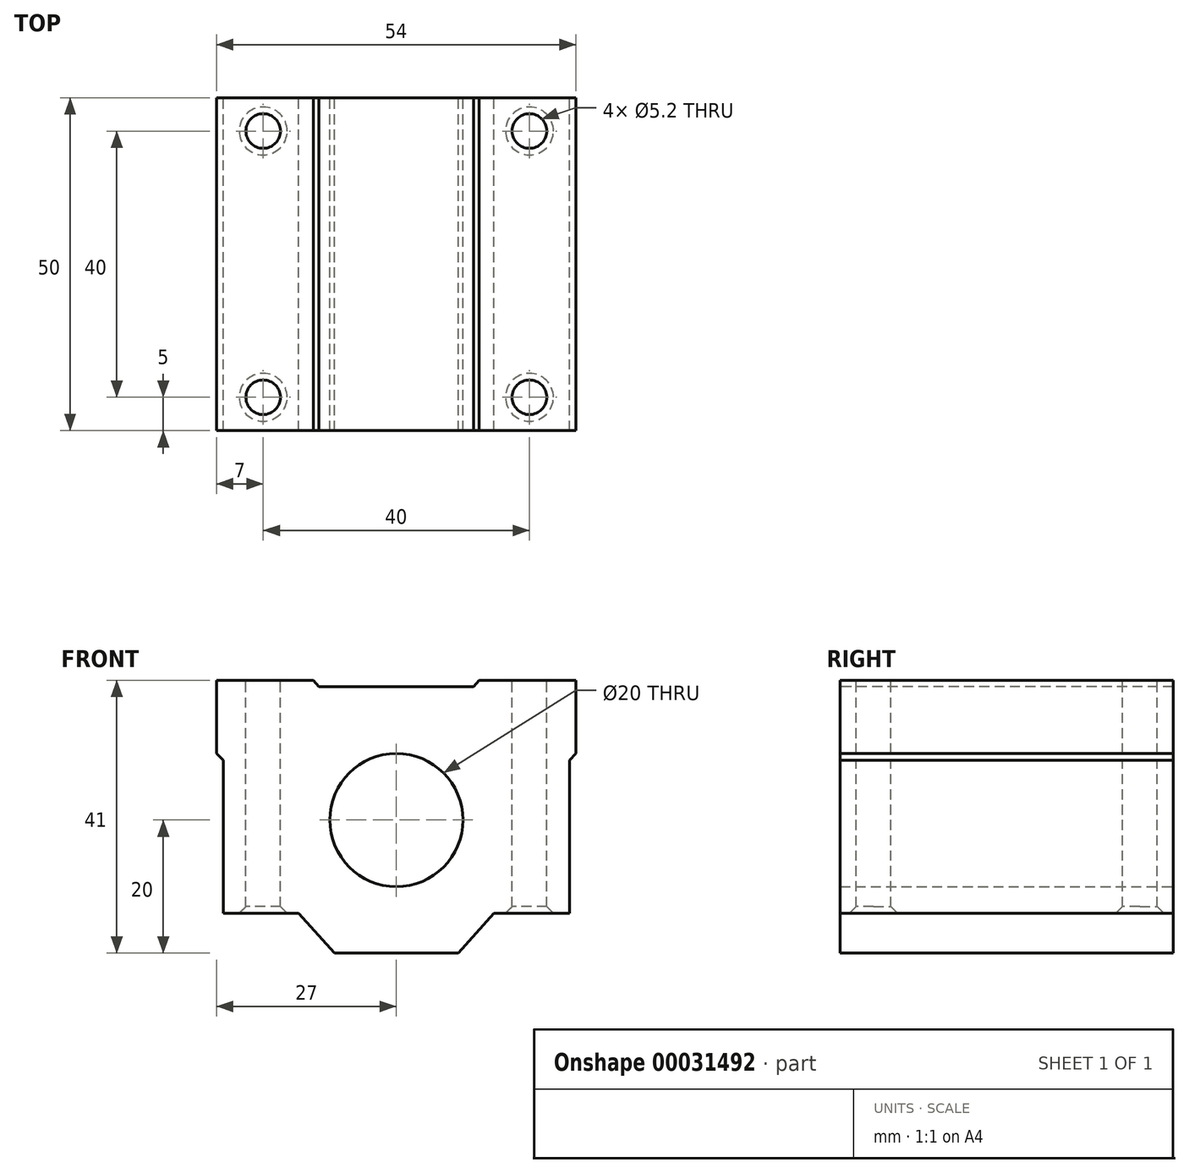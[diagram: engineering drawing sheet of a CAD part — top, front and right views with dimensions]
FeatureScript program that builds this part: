
annotation { "Feature Type Name" : "Feature", "Feature Type Description" : "" }
export const myFeature = defineFeature(function(context is Context, id is Id, definition is map)
    precondition{}
    {
        {
            var Q0;
            Q0=qCreatedBy(makeId("Front.planeOp"),FACE);
            var sketch = newSketch(context, id + "F0", { "sketchPlane" : qUnion([Q0])});
            skCircle(sketch, "E0", {"center": v(0, 0) * mm, "radius": 10 * mm});
            skLineSegment(sketch, "E1.rect.bottom", {"start": v(27, 21) * mm, "end": v(-27, 21) * mm});
            skLineSegment(sketch, "E1.rect.top", {"start": v(27, -20) * mm, "end": v(-27, -20) * mm});
            skLineSegment(sketch, "E1.rect.left", {"start": v(27, 21) * mm, "end": v(27, -20) * mm});
            skLineSegment(sketch, "E1.rect.right", {"start": v(-27, 21) * mm, "end": v(-27, -20) * mm});
            skPoint(sketch, "E1.rect.middle", {"position": v(0, 0.5) * mm});
            skLineSegment(sketch, "E2.0", {"start": v(27, 10) * mm, "end": v(-27, 10) * mm});
            skLineSegment(sketch, "E3.0", {"start": v(27, 9) * mm, "end": v(-27, 9) * mm});
            skLineSegment(sketch, "E4.0", {"start": v(27, -14) * mm, "end": v(-27, -14) * mm});
            skLineSegment(sketch, "E5.0", {"start": v(-26, 21) * mm, "end": v(-26, -20) * mm});
            skLineSegment(sketch, "E6.0", {"start": v(26, 21) * mm, "end": v(26, -20) * mm});
            skLineSegment(sketch, "E7", {"start": v(27, 10) * mm, "end": v(26, 9) * mm});
            skLineSegment(sketch, "E8", {"start": v(-27, 10) * mm, "end": v(-26, 9) * mm});
            skLineSegment(sketch, "E9", {"start": v(-14.67, -14) * mm, "end": v(-9.3, -20) * mm});
            skLineSegment(sketch, "E10.MirrorCS", {"start": v(14.67, -14) * mm, "end": v(9.3, -20) * mm});
            skPoint(sketch, "E11.orphan", {"position": v(16.75, -11.68) * mm});
            skPoint(sketch, "E12.orphan", {"position": v(5.82, -23.9) * mm});
            skPoint(sketch, "E13.orphan", {"position": v(-5.82, -23.9) * mm});
            skPoint(sketch, "E14.orphan", {"position": v(-16.75, -11.68) * mm});
            skSolve(sketch);
        }
        {
            var Q0;
            {var subQ3=sQuery(id+"F0.wireOp",EDGE,"E1.rect.bottom");var subQ5=sQuery(id+"F0.wireOp",EDGE,"E1.rect.left");var subQ7=makeQuery(id+"F0.imprint","INTERSECT",VERTEX,{"derivedFrom":[subQ3,subQ5]});Q0=makeQuery(id+"F0.imprint","IMPRINT",FACE,{"disambiguationData":[TD([[makeQuery(id+"F0.imprint","IMPRINT",EDGE,{"disambiguationData":[TD([[subQ7,-1.0]])],"derivedFrom":subQ3}),1.0]])]});}
            var Q1;
            {var subQ3=sQuery(id+"F0.wireOp",EDGE,"E1.rect.bottom");var subQ5=sQuery(id+"F0.wireOp",EDGE,"E1.rect.right");var subQ7=makeQuery(id+"F0.imprint","INTERSECT",VERTEX,{"derivedFrom":[subQ3,subQ5]});Q1=makeQuery(id+"F0.imprint","IMPRINT",FACE,{"disambiguationData":[TD([[makeQuery(id+"F0.imprint","IMPRINT",EDGE,{"disambiguationData":[TD([[subQ7,1.0]])],"derivedFrom":subQ3}),1.0]])]});}
            var Q2;
            {var subQ1=sQuery(id+"F0.wireOp",EDGE,"E9");Q2=makeQuery(id+"F0.imprint","IMPRINT",FACE,{"disambiguationData":[TD([[makeQuery(id+"F0.imprint","IMPRINT",EDGE,{"derivedFrom":subQ1}),1.0]])]});}
            var Q3;
            {var subQ0=sQuery(id+"F0.wireOp",EDGE,"E7");Q3=makeQuery(id+"F0.imprint","IMPRINT",FACE,{"disambiguationData":[TD([[makeQuery(id+"F0.imprint","IMPRINT",EDGE,{"derivedFrom":subQ0}),-1.0]])]});}
            var Q4;
            {var subQ0=sQuery(id+"F0.wireOp",EDGE,"E8");Q4=makeQuery(id+"F0.imprint","IMPRINT",FACE,{"disambiguationData":[TD([[makeQuery(id+"F0.imprint","IMPRINT",EDGE,{"derivedFrom":subQ0}),1.0]])]});}
            var Q5;
            {var subQ3=sQuery(id+"F0.wireOp",EDGE,"E3.0");var subQ10=sQuery(id+"F0.wireOp",EDGE,"E0");var subQ11=makeQuery(id+"F0.imprint","INTERSECT",VERTEX,{"disambiguationData":[OD(0.0)],"derivedFrom":[subQ10,subQ3]});Q5=makeQuery(id+"F0.imprint","IMPRINT",FACE,{"disambiguationData":[TD([[makeQuery(id+"F0.imprint","IMPRINT",EDGE,{"disambiguationData":[TD([[subQ11,1.0]])],"derivedFrom":subQ10}),-1.0]])]});}
            var Q6;
            {var subQ1=sQuery(id+"F0.wireOp",EDGE,"E0");var subQ5=sQuery(id+"F0.wireOp",EDGE,"E2.0");var subQ7=makeQuery(id+"F0.imprint","INTERSECT",VERTEX,{"derivedFrom":[subQ1,subQ5]});Q6=makeQuery(id+"F0.imprint","IMPRINT",FACE,{"disambiguationData":[TD([[makeQuery(id+"F0.imprint","IMPRINT",EDGE,{"disambiguationData":[TD([[subQ7,-1.0]])],"derivedFrom":subQ1}),-1.0]])]});}
            var Q7;
            {var subQ3=sQuery(id+"F0.wireOp",EDGE,"E1.rect.bottom");var subQ5=sQuery(id+"F0.wireOp",EDGE,"E5.0");var subQ6=makeQuery(id+"F0.imprint","INTERSECT",VERTEX,{"derivedFrom":[subQ3,subQ5]});Q7=makeQuery(id+"F0.imprint","IMPRINT",FACE,{"disambiguationData":[TD([[makeQuery(id+"F0.imprint","IMPRINT",EDGE,{"disambiguationData":[TD([[subQ6,1.0]])],"derivedFrom":subQ3}),1.0]])]});}
            var Q8;
            {var subQ1=sQuery(id+"F0.wireOp",EDGE,"E0");var subQ5=sQuery(id+"F0.wireOp",EDGE,"E2.0");var subQ7=makeQuery(id+"F0.imprint","INTERSECT",VERTEX,{"derivedFrom":[subQ1,subQ5]});Q8=makeQuery(id+"F0.imprint","IMPRINT",FACE,{"disambiguationData":[TD([[makeQuery(id+"F0.imprint","IMPRINT",EDGE,{"disambiguationData":[TD([[subQ7,1.0]])],"derivedFrom":subQ1}),-1.0]])]});}
            extrude(context, id + "F1", {"entities" : qUnion([Q0, Q1, Q2, Q3, Q4, Q5, Q6, Q7, Q8]), "depth" : 50 * mm, "symmetric" : true});
        }
        {
            var Q0;
            Q0=qCreatedBy(makeId("Front.planeOp"),FACE);
            var sketch = newSketch(context, id + "F2", { "sketchPlane" : qUnion([Q0])});
            skLineSegment(sketch, "E15.0", {"start": v(27, 21) * mm, "end": v(-27, 21) * mm});
            skLineSegment(sketch, "E16.0", {"start": v(27, 20) * mm, "end": v(-27, 20) * mm});
            skLineSegment(sketch, "E17", {"start": v(-11.6, 20) * mm, "end": v(-12.44, 21) * mm});
            skLineSegment(sketch, "E18.MirrorCS", {"start": v(11.6, 20) * mm, "end": v(12.44, 21) * mm});
            skPoint(sketch, "E19.orphan", {"position": v(13.28, 22) * mm});
            skPoint(sketch, "E20.orphan", {"position": v(10.73, 18.95) * mm});
            skPoint(sketch, "E21.orphan", {"position": v(-10.73, 18.95) * mm});
            skPoint(sketch, "E22.orphan", {"position": v(-13.28, 22) * mm});
            skSolve(sketch);
        }
        {
            var Q0;
            Q0 = qSketchRegion(id + "F2", true);
            extrude(context, id + "F3", {"entities" : qUnion([Q0]), "operationType" : NewBodyOperationType.REMOVE, "oppositeDirection" : true, "depth" : 100 * mm, "symmetric" : true});
        }
        {
            var Q0;
            Q0=makeQuery(id+"F1.opExtrude","SWEPT_FACE",FACE,{"disambiguationData":[OSD([sQuery(id+"F0.wireOp",EDGE,"E1.rect.bottom")])]});
            var sketch = newSketch(context, id + "F4", { "sketchPlane" : qUnion([Q0])});
            skLineSegment(sketch, "E23.rect.bottom", {"start": v(20, 20) * mm, "end": v(-20, 20) * mm, "construction": true});
            skLineSegment(sketch, "E23.rect.top", {"start": v(20, -20) * mm, "end": v(-20, -20) * mm, "construction": true});
            skLineSegment(sketch, "E23.rect.left", {"start": v(20, 20) * mm, "end": v(20, -20) * mm, "construction": true});
            skLineSegment(sketch, "E23.rect.right", {"start": v(-20, 20) * mm, "end": v(-20, -20) * mm, "construction": true});
            skPoint(sketch, "E23.rect.middle", {"position": v(0, 0) * mm});
            skCircle(sketch, "E24", {"center": v(-20, -20) * mm, "radius": 2.6 * mm});
            skCircle(sketch, "E25", {"center": v(-20, 20) * mm, "radius": 2.6 * mm});
            skCircle(sketch, "E26", {"center": v(20, 20) * mm, "radius": 2.6 * mm});
            skCircle(sketch, "E27", {"center": v(20, -20) * mm, "radius": 2.6 * mm});
            skSolve(sketch);
        }
        {
            var Q0;
            Q0=makeQuery(id+"F4.imprint","IMPRINT",FACE,{"disambiguationData":[TD([[makeQuery(id+"F4.imprint","IMPRINT",EDGE,{"derivedFrom":sQuery(id+"F4.wireOp",EDGE,"E26")}),1.0]])]});
            var Q1;
            Q1=makeQuery(id+"F4.imprint","IMPRINT",FACE,{"disambiguationData":[TD([[makeQuery(id+"F4.imprint","IMPRINT",EDGE,{"derivedFrom":sQuery(id+"F4.wireOp",EDGE,"E25")}),1.0]])]});
            var Q2;
            Q2=makeQuery(id+"F4.imprint","IMPRINT",FACE,{"disambiguationData":[TD([[makeQuery(id+"F4.imprint","IMPRINT",EDGE,{"derivedFrom":sQuery(id+"F4.wireOp",EDGE,"E24")}),1.0]])]});
            var Q3;
            Q3=makeQuery(id+"F4.imprint","IMPRINT",FACE,{"disambiguationData":[TD([[makeQuery(id+"F4.imprint","IMPRINT",EDGE,{"derivedFrom":sQuery(id+"F4.wireOp",EDGE,"E27")}),1.0]])]});
            extrude(context, id + "F5", {"entities" : qUnion([Q0, Q1, Q2, Q3]), "operationType" : NewBodyOperationType.REMOVE, "endBound" : BoundingType.THROUGH_ALL, "oppositeDirection" : true, "depth" : 25 * mm});
        }
        {
            var Q0;
            Q0=makeQuery(id+"F5.boolean.opBoolean","COPY",EDGE,{"derivedFrom":makeQuery(id+"F5.opExtrude","CAP_EDGE",EDGE,{"disambiguationData":[OSD([sQuery(id+"F4.wireOp",EDGE,"E27")])],"isStart":true})});
            var Q1;
            Q1=makeQuery(id+"F5.boolean.opBoolean","COPY",EDGE,{"derivedFrom":makeQuery(id+"F5.opExtrude","CAP_EDGE",EDGE,{"disambiguationData":[OSD([sQuery(id+"F4.wireOp",EDGE,"E24")])],"isStart":true})});
            var Q2;
            Q2=makeQuery(id+"F5.boolean.opBoolean","COPY",EDGE,{"derivedFrom":makeQuery(id+"F5.opExtrude","CAP_EDGE",EDGE,{"disambiguationData":[OSD([sQuery(id+"F4.wireOp",EDGE,"E25")])],"isStart":true})});
            var Q3;
            Q3=makeQuery(id+"F5.boolean.opBoolean","COPY",EDGE,{"derivedFrom":makeQuery(id+"F5.opExtrude","CAP_EDGE",EDGE,{"disambiguationData":[OSD([sQuery(id+"F4.wireOp",EDGE,"E26")])],"isStart":true})});
            var Q4;
            {var subQ0=sQuery(id+"F0.wireOp",EDGE,"E4.0");Q4=makeQuery(id+"F5.boolean.opBoolean","INTERSECT",EDGE,{"derivedFrom":[makeQuery(id+"F1.opExtrude","SWEPT_FACE",FACE,{"disambiguationData":[OSD([subQ0]),TDD([makeQuery(id+"F0.imprint","IMPRINT",EDGE,{"disambiguationData":[TD([[makeQuery(id+"F0.imprint","INTERSECT",VERTEX,{"derivedFrom":[subQ0,sQuery(id+"F0.wireOp",EDGE,"E10.MirrorCS")]}),1.0]])],"derivedFrom":subQ0})])]}),makeQuery(id+"F5.opExtrude","SWEPT_FACE",FACE,{"disambiguationData":[OSD([sQuery(id+"F4.wireOp",EDGE,"E26")])]})]});}
            var Q5;
            {var subQ0=sQuery(id+"F0.wireOp",EDGE,"E4.0");Q5=makeQuery(id+"F5.boolean.opBoolean","INTERSECT",EDGE,{"derivedFrom":[makeQuery(id+"F1.opExtrude","SWEPT_FACE",FACE,{"disambiguationData":[OSD([subQ0]),TDD([makeQuery(id+"F0.imprint","IMPRINT",EDGE,{"disambiguationData":[TD([[makeQuery(id+"F0.imprint","INTERSECT",VERTEX,{"derivedFrom":[subQ0,sQuery(id+"F0.wireOp",EDGE,"E9")]}),-1.0]])],"derivedFrom":subQ0})])]}),makeQuery(id+"F5.opExtrude","SWEPT_FACE",FACE,{"disambiguationData":[OSD([sQuery(id+"F4.wireOp",EDGE,"E25")])]})]});}
            var Q6;
            {var subQ0=sQuery(id+"F0.wireOp",EDGE,"E4.0");Q6=makeQuery(id+"F5.boolean.opBoolean","INTERSECT",EDGE,{"derivedFrom":[makeQuery(id+"F1.opExtrude","SWEPT_FACE",FACE,{"disambiguationData":[OSD([subQ0]),TDD([makeQuery(id+"F0.imprint","IMPRINT",EDGE,{"disambiguationData":[TD([[makeQuery(id+"F0.imprint","INTERSECT",VERTEX,{"derivedFrom":[subQ0,sQuery(id+"F0.wireOp",EDGE,"E10.MirrorCS")]}),1.0]])],"derivedFrom":subQ0})])]}),makeQuery(id+"F5.opExtrude","SWEPT_FACE",FACE,{"disambiguationData":[OSD([sQuery(id+"F4.wireOp",EDGE,"E27")])]})]});}
            var Q7;
            {var subQ0=sQuery(id+"F0.wireOp",EDGE,"E4.0");Q7=makeQuery(id+"F5.boolean.opBoolean","INTERSECT",EDGE,{"derivedFrom":[makeQuery(id+"F1.opExtrude","SWEPT_FACE",FACE,{"disambiguationData":[OSD([subQ0]),TDD([makeQuery(id+"F0.imprint","IMPRINT",EDGE,{"disambiguationData":[TD([[makeQuery(id+"F0.imprint","INTERSECT",VERTEX,{"derivedFrom":[subQ0,sQuery(id+"F0.wireOp",EDGE,"E9")]}),-1.0]])],"derivedFrom":subQ0})])]}),makeQuery(id+"F5.opExtrude","SWEPT_FACE",FACE,{"disambiguationData":[OSD([sQuery(id+"F4.wireOp",EDGE,"E24")])]})]});}
            chamfer(context, id + "F6", {"entities" : qUnion([Q0, Q1, Q2, Q3, Q4, Q5, Q6, Q7]), "width" : 1 * mm, "tangentPropagation" : true});
        }
    });
